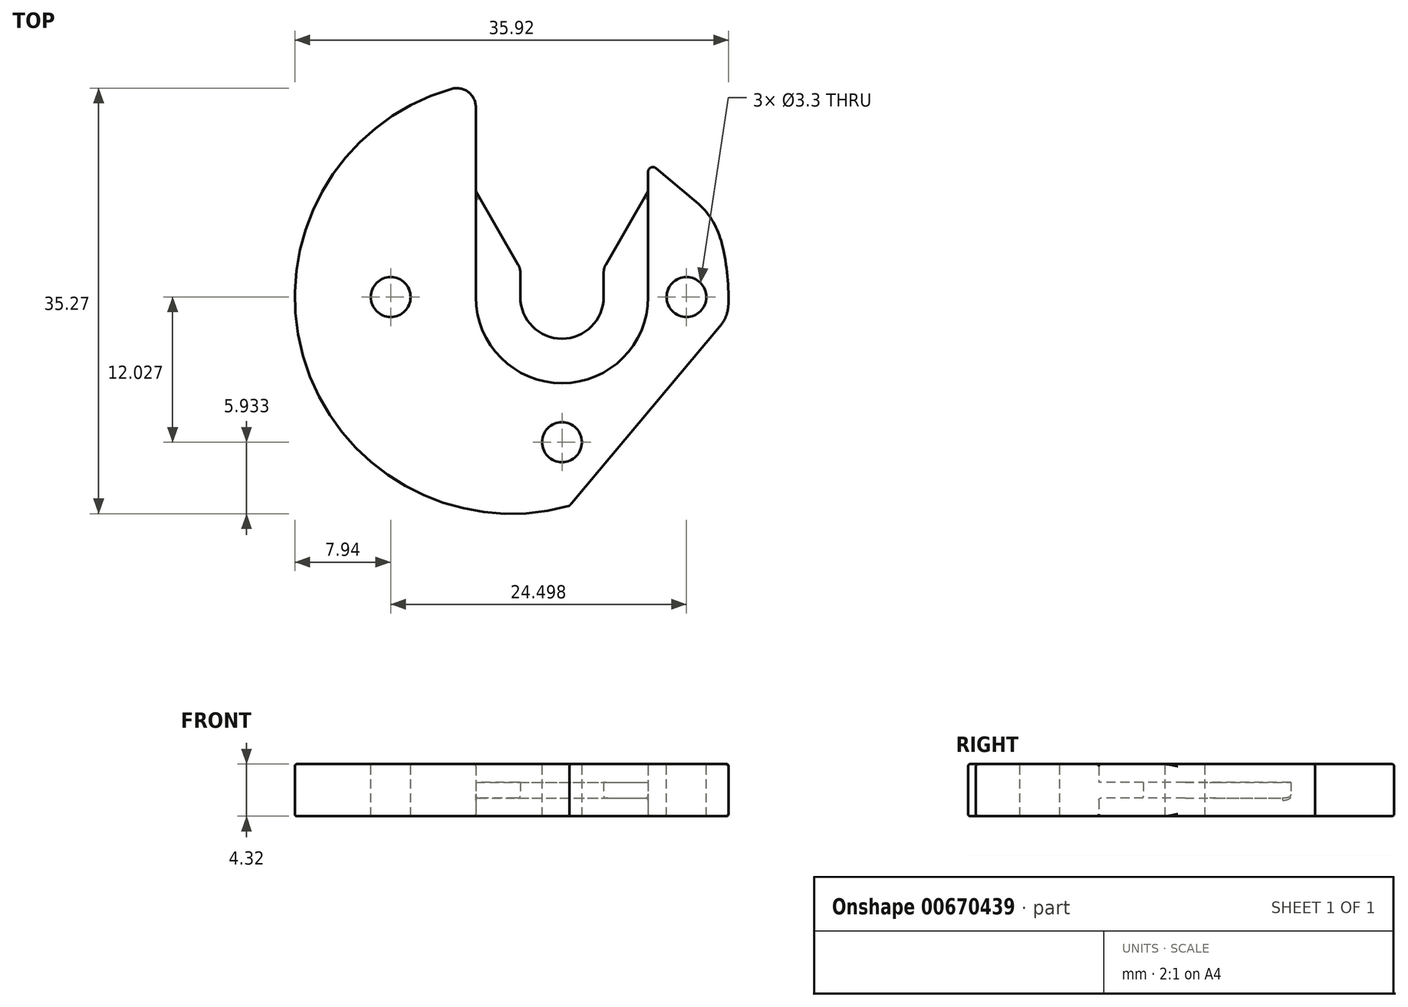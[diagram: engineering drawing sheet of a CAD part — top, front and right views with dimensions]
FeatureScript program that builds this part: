
annotation { "Feature Type Name" : "Feature", "Feature Type Description" : "" }
export const myFeature = defineFeature(function(context is Context, id is Id, definition is map)
    precondition{}
    {
        {
            var Q0;
            Q0=qCreatedBy(makeId("Top.planeOp"),FACE);
            var sketch = newSketch(context, id + "F0", { "sketchPlane" : qUnion([Q0])});
            skArc(sketch, "E0", {"start": v(-4.98, 17.25) * mm, "mid": v(-8.82, -15.64) * mm, "end": v(17.34, 4.66) * mm});
            skLineSegment(sketch, "E1", {"start": v(-2.97, 15.74) * mm, "end": v(-2.97, 0) * mm});
            skLineSegment(sketch, "E2.0", {"start": v(11.3, 10.38) * mm, "end": v(11.3, 0) * mm});
            skArc(sketch, "E3", {"start": v(-2.97, 0) * mm, "mid": v(4.17, -7.14) * mm, "end": v(11.3, 0) * mm});
            skPoint(sketch, "E4.visualSharp", {"position": v(-2.97, 17.71) * mm});
            skArc(sketch, "E4.filletArc", {"start": v(-2.97, 15.74) * mm, "mid": v(-3.6, 17) * mm, "end": v(-4.98, 17.25) * mm});
            skLineSegment(sketch, "E5", {"start": v(11.95, 10.68) * mm, "end": v(15.3, 7.88) * mm});
            skPoint(sketch, "E6.visualSharp", {"position": v(11.3, 11.22) * mm});
            skArc(sketch, "E6.filletArc", {"start": v(11.95, 10.68) * mm, "mid": v(11.53, 10.74) * mm, "end": v(11.3, 10.38) * mm});
            skPoint(sketch, "E7.visualSharp", {"position": v(16.64, 6.74) * mm});
            skArc(sketch, "E7.filletArc", {"start": v(17.34, 4.66) * mm, "mid": v(16.56, 6.43) * mm, "end": v(15.3, 7.88) * mm});
            skSolve(sketch);
        }
        {
            var Q0;
            Q0=makeQuery(id+"F0.imprint","IMPRINT",FACE,{"disambiguationData":[TD([[makeQuery(id+"F0.imprint","IMPRINT",EDGE,{"derivedFrom":sQuery(id+"F0.wireOp",EDGE,"E0")}),1.0]])]});
            extrude(context, id + "F1", {"entities" : qUnion([Q0]), "depth" : 2.16 * mm, "offsetDistance" : 25.4 * mm, "hasSecondDirection" : true, "secondDirectionOppositeDirection" : true, "secondDirectionDepth" : 2.16 * mm});
        }
        {
            var Q0;
            Q0=qCreatedBy(makeId("Top.planeOp"),FACE);
            var sketch = newSketch(context, id + "F2", { "sketchPlane" : qUnion([Q0])});
            skArc(sketch, "E8.0", {"start": v(0.71, 0) * mm, "mid": v(4.17, -3.45) * mm, "end": v(7.62, 0) * mm});
            skLineSegment(sketch, "E9", {"start": v(0.71, 0) * mm, "end": v(0.71, 2.05) * mm});
            skLineSegment(sketch, "E10", {"start": v(0.54, 2.68) * mm, "end": v(-2.97, 8.77) * mm});
            skLineSegment(sketch, "E11", {"start": v(4.17, 0) * mm, "end": v(4.17, 5.85) * mm, "construction": true});
            skLineSegment(sketch, "E12.MirrorCS", {"start": v(7.62, 0) * mm, "end": v(7.62, 2.05) * mm});
            skLineSegment(sketch, "E13.MirrorCS", {"start": v(7.8, 2.68) * mm, "end": v(11.3, 8.77) * mm});
            skPoint(sketch, "E14.visualSharp", {"position": v(0.71, 2.39) * mm});
            skArc(sketch, "E14.filletArc", {"start": v(0.71, 2.05) * mm, "mid": v(0.67, 2.38) * mm, "end": v(0.54, 2.68) * mm});
            skPoint(sketch, "E15.visualSharp", {"position": v(7.62, 2.39) * mm});
            skArc(sketch, "E15.filletArc", {"start": v(7.8, 2.68) * mm, "mid": v(7.66, 2.38) * mm, "end": v(7.62, 2.05) * mm});
            skLineSegment(sketch, "E16", {"start": v(-2.97, 8.77) * mm, "end": v(-2.97, 0) * mm});
            skArc(sketch, "E17.0", {"start": v(-2.97, 0) * mm, "mid": v(4.17, -7.14) * mm, "end": v(11.3, 0) * mm});
            skLineSegment(sketch, "E18", {"start": v(11.3, 0) * mm, "end": v(11.3, 8.77) * mm});
            skSolve(sketch);
        }
        {
            var Q0;
            Q0=makeQuery(id+"F2.imprint","IMPRINT",FACE,{"disambiguationData":[TD([[makeQuery(id+"F2.imprint","IMPRINT",EDGE,{"derivedFrom":sQuery(id+"F2.wireOp",EDGE,"E8.0")}),-1.0]])]});
            extrude(context, id + "F3", {"entities" : qUnion([Q0]), "operationType" : NewBodyOperationType.ADD, "depth" : 0.66 * mm, "offsetDistance" : 25.4 * mm, "hasSecondDirection" : true, "secondDirectionOppositeDirection" : true, "secondDirectionDepth" : 0.66 * mm});
        }
        {
            var Q0;
            Q0=makeQuery(id+"F3.opExtrude","CAP_EDGE",EDGE,{"disambiguationData":[OSD([sQuery(id+"F2.wireOp",EDGE,"E17.0")])],"isStart":true});
            var Q1;
            Q1=makeQuery(id+"F3.opExtrude","CAP_EDGE",EDGE,{"disambiguationData":[OSD([sQuery(id+"F2.wireOp",EDGE,"E17.0")])],"isStart":false});
            var Q2;
            Q2=makeQuery(id+"F3.opExtrude","SWEPT_EDGE",EDGE,{"disambiguationData":[OSD([sQuery(id+"F2.wireOp",EDGE,"E10"),sQuery(id+"F2.wireOp",EDGE,"E16")])]});
            var Q3;
            Q3=makeQuery(id+"F3.opExtrude","SWEPT_EDGE",EDGE,{"disambiguationData":[OSD([sQuery(id+"F2.wireOp",EDGE,"E13.MirrorCS"),sQuery(id+"F2.wireOp",EDGE,"E18")])]});
            var Q4;
            Q4=makeQuery(id+"F1.opExtrude","CAP_FACE",FACE,{"disambiguationData":[OSD([sQuery(id+"F0.wireOp",EDGE,"E0"),sQuery(id+"F0.wireOp",EDGE,"E1"),sQuery(id+"F0.wireOp",EDGE,"E2.0"),sQuery(id+"F0.wireOp",EDGE,"E3"),sQuery(id+"F0.wireOp",EDGE,"E4.filletArc"),sQuery(id+"F0.wireOp",EDGE,"8914ef62-5daa-4641-99c7-5d31eb944ef2.filletArc")])],"isStart":false});
            var Q5;
            Q5=makeQuery(id+"F1.opExtrude","CAP_EDGE",EDGE,{"disambiguationData":[OSD([sQuery(id+"F0.wireOp",EDGE,"E0")])],"isStart":true});
            var Q6;
            Q6=makeQuery(id+"F1.opExtrude","CAP_EDGE",EDGE,{"disambiguationData":[OSD([sQuery(id+"F0.wireOp",EDGE,"E1")])],"isStart":true});
            var Q7;
            Q7=makeQuery(id+"F3.opExtrude","CAP_EDGE",EDGE,{"disambiguationData":[OSD([sQuery(id+"F2.wireOp",EDGE,"E16")])],"isStart":true});
            var Q8;
            Q8=makeQuery(id+"F3.opExtrude","CAP_EDGE",EDGE,{"disambiguationData":[OSD([sQuery(id+"F2.wireOp",EDGE,"E10")])],"isStart":true});
            var Q9;
            Q9=makeQuery(id+"F1.opExtrude","CAP_FACE",FACE,{"disambiguationData":[OSD([sQuery(id+"F0.wireOp",EDGE,"E0"),sQuery(id+"F0.wireOp",EDGE,"E1"),sQuery(id+"F0.wireOp",EDGE,"E2.0"),sQuery(id+"F0.wireOp",EDGE,"E3"),sQuery(id+"F0.wireOp",EDGE,"E4.filletArc"),sQuery(id+"F0.wireOp",EDGE,"8914ef62-5daa-4641-99c7-5d31eb944ef2.filletArc")])],"isStart":true});
            fillet(context, id + "F4", {"entities" : qUnion([Q0, Q1, Q2, Q3, Q4, Q5, Q6, Q7, Q8, Q9]), "radius" : 0.18 * mm, "tangentPropagation" : true, "allowEdgeOverflow" : false});
        }
        {
            var Q0;
            Q0=makeQuery(id+"F1.opExtrude","CAP_FACE",FACE,{"disambiguationData":[OSD([sQuery(id+"F0.wireOp",EDGE,"E0"),sQuery(id+"F0.wireOp",EDGE,"E1"),sQuery(id+"F0.wireOp",EDGE,"E2.0"),sQuery(id+"F0.wireOp",EDGE,"E3"),sQuery(id+"F0.wireOp",EDGE,"E4.filletArc"),sQuery(id+"F0.wireOp",EDGE,"8914ef62-5daa-4641-99c7-5d31eb944ef2.filletArc")])],"isStart":false});
            var sketch = newSketch(context, id + "F5", { "sketchPlane" : qUnion([Q0])});
            skPoint(sketch, "E19", {"position": v(-10.02, 0) * mm});
            skPoint(sketch, "E20", {"position": v(14.48, 0) * mm});
            skPoint(sketch, "E21", {"position": v(4.17, -12.03) * mm});
            skPoint(sketch, "E22", {"position": v(4.17, 0) * mm});
            skCircle(sketch, "E23", {"center": v(-10.02, 0) * mm, "radius": 1.65 * mm});
            skCircle(sketch, "E24", {"center": v(4.17, -12.03) * mm, "radius": 1.65 * mm});
            skCircle(sketch, "E25", {"center": v(14.48, 0) * mm, "radius": 1.65 * mm});
            skSolve(sketch);
        }
        {
            var Q0;
            Q0=makeQuery(id+"F5.imprint","IMPRINT",FACE,{"disambiguationData":[TD([[makeQuery(id+"F5.imprint","IMPRINT",EDGE,{"derivedFrom":sQuery(id+"F5.wireOp",EDGE,"E23")}),1.0]])]});
            var Q1;
            Q1=makeQuery(id+"F5.imprint","IMPRINT",FACE,{"disambiguationData":[TD([[makeQuery(id+"F5.imprint","IMPRINT",EDGE,{"derivedFrom":sQuery(id+"F5.wireOp",EDGE,"E24")}),1.0]])]});
            var Q2;
            Q2=makeQuery(id+"F5.imprint","IMPRINT",FACE,{"disambiguationData":[TD([[makeQuery(id+"F5.imprint","IMPRINT",EDGE,{"derivedFrom":sQuery(id+"F5.wireOp",EDGE,"E25")}),1.0]])]});
            extrude(context, id + "F6", {"entities" : qUnion([Q0, Q1, Q2]), "operationType" : NewBodyOperationType.REMOVE, "endBound" : BoundingType.THROUGH_ALL, "oppositeDirection" : true, "depth" : 25.4 * mm, "offsetDistance" : 25.4 * mm});
        }
        {
            var Q0;
            Q0=makeQuery(id+"F1.opExtrude","CAP_FACE",FACE,{"disambiguationData":[OSD([sQuery(id+"F0.wireOp",EDGE,"E0"),sQuery(id+"F0.wireOp",EDGE,"E1"),sQuery(id+"F0.wireOp",EDGE,"E2.0"),sQuery(id+"F0.wireOp",EDGE,"E3"),sQuery(id+"F0.wireOp",EDGE,"E4.filletArc"),sQuery(id+"F0.wireOp",EDGE,"E5"),sQuery(id+"F0.wireOp",EDGE,"E6.filletArc"),sQuery(id+"F0.wireOp",EDGE,"E7.filletArc")])],"isStart":false});
            var sketch = newSketch(context, id + "F7", { "sketchPlane" : qUnion([Q0])});
            skArc(sketch, "E26.0", {"start": v(17.88, -1.7) * mm, "mid": v(13.76, -11.54) * mm, "end": v(4.77, -17.31) * mm});
            skLineSegment(sketch, "E27", {"start": v(17.88, -1.7) * mm, "end": v(4.77, -17.31) * mm});
            skPoint(sketch, "E28.orphan", {"position": v(17.34, 4.66) * mm});
            skPoint(sketch, "E29.orphan", {"position": v(-4.98, 17.25) * mm});
            skSolve(sketch);
        }
        {
            var Q0;
            Q0 = qSketchRegion(id + "F7", true);
            extrude(context, id + "F8", {"entities" : qUnion([Q0]), "operationType" : NewBodyOperationType.REMOVE, "endBound" : BoundingType.THROUGH_ALL, "oppositeDirection" : true, "depth" : 25.4 * mm, "offsetDistance" : 25.4 * mm});
        }
        {
            var Q0;
            {var subQ0=sQuery(id+"F7.wireOp",EDGE,"E27");var subQ1=sQuery(id+"F7.wireOp",EDGE,"E26.0");Q0=makeQuery(id+"F8.boolean.opBoolean","COPY",EDGE,{"derivedFrom":makeQuery(id+"F8.opExtrude","SWEPT_EDGE",EDGE,{"disambiguationData":[OSD([subQ1,subQ0]),TDD([makeQuery(id+"F7.imprint","INTERSECT",VERTEX,{"disambiguationData":[OD(0.0)],"derivedFrom":[subQ1,subQ0]})])]})});}
            var Q1;
            {var subQ0=sQuery(id+"F7.wireOp",EDGE,"E27");var subQ1=sQuery(id+"F7.wireOp",EDGE,"E26.0");Q1=makeQuery(id+"F8.boolean.opBoolean","COPY",EDGE,{"derivedFrom":makeQuery(id+"F8.opExtrude","SWEPT_EDGE",EDGE,{"disambiguationData":[OSD([subQ1,subQ0]),TDD([makeQuery(id+"F7.imprint","INTERSECT",VERTEX,{"disambiguationData":[OD(1.0)],"derivedFrom":[subQ1,subQ0]})])]})});}
            fillet(context, id + "F9", {"entities" : qUnion([Q0, Q1]), "radius" : 3.05 * mm, "allowEdgeOverflow" : false});
        }
    });
